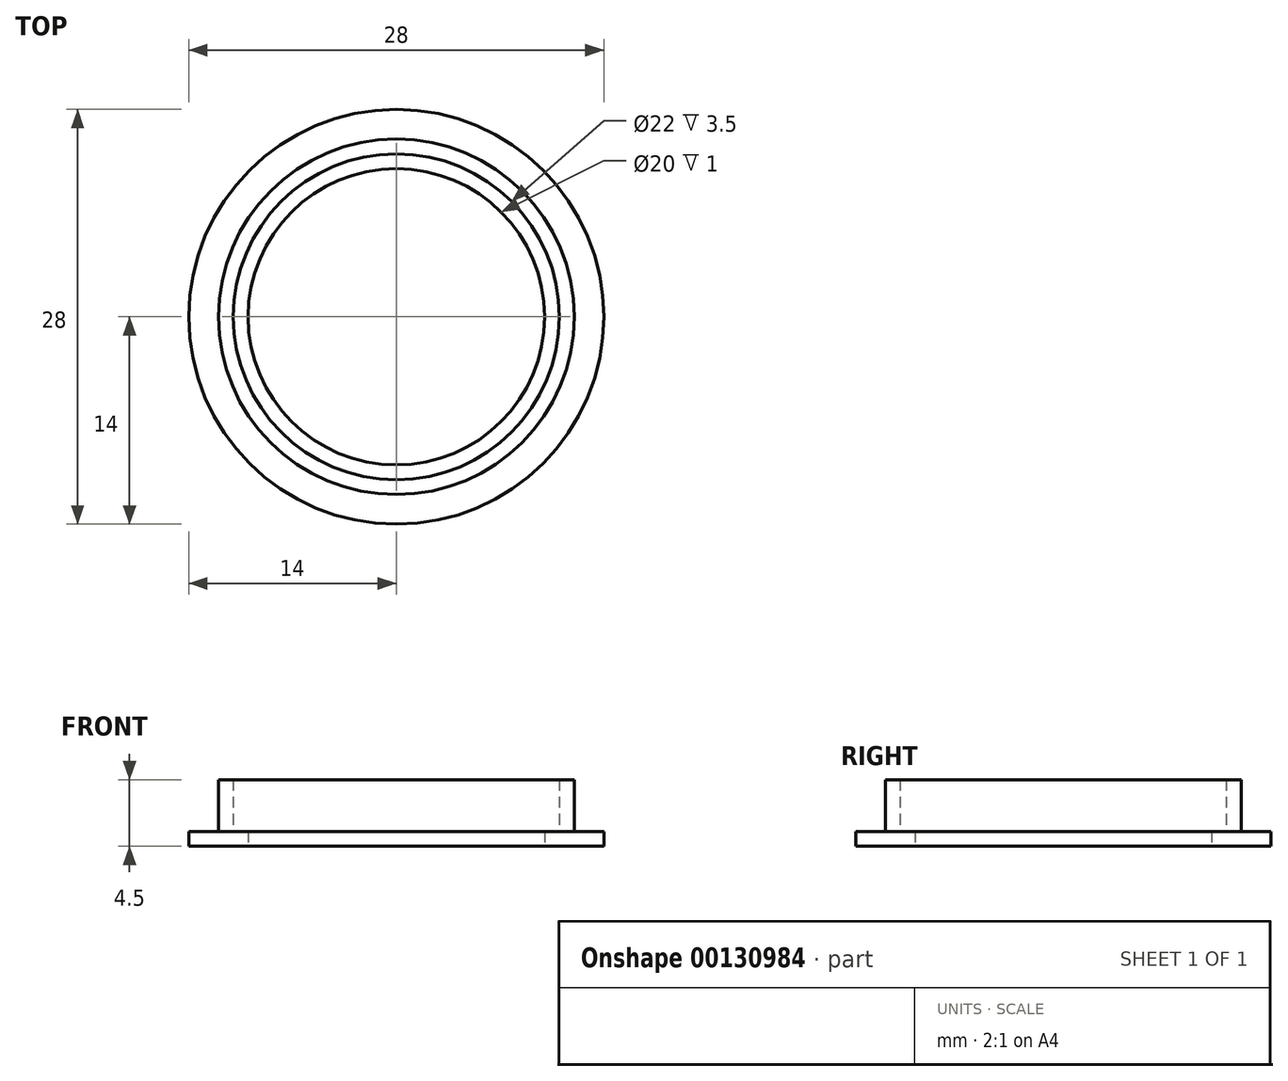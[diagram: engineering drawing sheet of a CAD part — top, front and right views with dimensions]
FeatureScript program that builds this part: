
annotation { "Feature Type Name" : "Feature", "Feature Type Description" : "" }
export const myFeature = defineFeature(function(context is Context, id is Id, definition is map)
    precondition{}
    {
        {
            var Q0;
            Q0=qCreatedBy(makeId("Top.planeOp"),FACE);
            var sketch = newSketch(context, id + "F0", { "sketchPlane" : qUnion([Q0])});
            skCircle(sketch, "E0", {"center": v(0, 0) * mm, "radius": 11 * mm});
            skCircle(sketch, "E1", {"center": v(0, 0) * mm, "radius": 14 * mm});
            skCircle(sketch, "E2.0", {"center": v(0, 0) * mm, "radius": 10 * mm});
            skCircle(sketch, "E3.0", {"center": v(0, 0) * mm, "radius": 12 * mm});
            skSolve(sketch);
        }
        {
            var Q0;
            Q0=makeQuery(id+"F0.imprint","IMPRINT",FACE,{"disambiguationData":[TD([[makeQuery(id+"F0.imprint","IMPRINT",EDGE,{"derivedFrom":sQuery(id+"F0.wireOp",EDGE,"E0")}),-1.0]])]});
            extrude(context, id + "F1", {"entities" : qUnion([Q0]), "depth" : 4.5 * mm});
        }
        {
            var Q0;
            Q0=makeQuery(id+"F0.imprint","IMPRINT",FACE,{"disambiguationData":[TD([[makeQuery(id+"F0.imprint","IMPRINT",EDGE,{"derivedFrom":sQuery(id+"F0.wireOp",EDGE,"E0")}),1.0]])]});
            var Q1;
            Q1=makeQuery(id+"F0.imprint","IMPRINT",FACE,{"disambiguationData":[TD([[makeQuery(id+"F0.imprint","IMPRINT",EDGE,{"derivedFrom":sQuery(id+"F0.wireOp",EDGE,"E1")}),1.0]])]});
            extrude(context, id + "F2", {"entities" : qUnion([Q0, Q1]), "operationType" : NewBodyOperationType.ADD, "depth" : 1 * mm});
        }
    });
